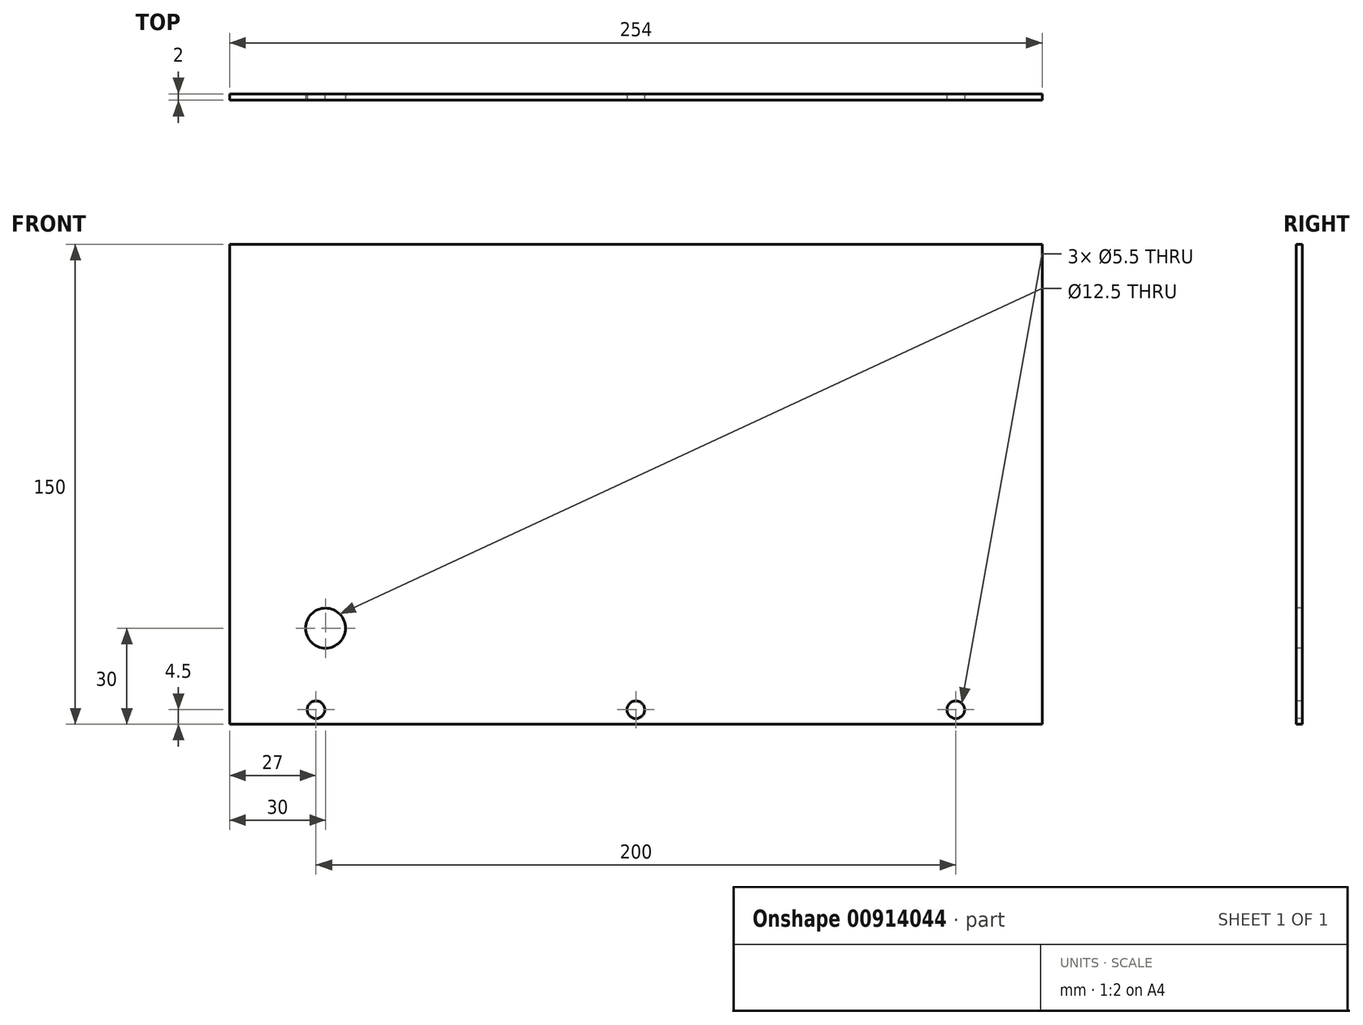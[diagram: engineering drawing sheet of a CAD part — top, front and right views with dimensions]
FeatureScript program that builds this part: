
annotation { "Feature Type Name" : "Feature", "Feature Type Description" : "" }
export const myFeature = defineFeature(function(context is Context, id is Id, definition is map)
    precondition{}
    {
        {
            var Q0;
            Q0=qCreatedBy(makeId("Front.planeOp"),FACE);
            var sketch = newSketch(context, id + "F0", { "sketchPlane" : qUnion([Q0])});
            skLineSegment(sketch, "E0.bottom", {"start": v(-127, 75) * mm, "end": v(127, 75) * mm});
            skLineSegment(sketch, "E0.top", {"start": v(-127, -75) * mm, "end": v(127, -75) * mm});
            skLineSegment(sketch, "E0.left", {"start": v(-127, 75) * mm, "end": v(-127, -75) * mm});
            skLineSegment(sketch, "E0.right", {"start": v(127, 75) * mm, "end": v(127, -75) * mm});
            skPoint(sketch, "E0.middle", {"position": v(0, 0) * mm});
            skSolve(sketch);
        }
        {
            var Q0;
            Q0=makeQuery(id+"F0.imprint","IMPRINT",FACE,{"disambiguationData":[TD([[makeQuery(id+"F0.imprint","IMPRINT",EDGE,{"derivedFrom":sQuery(id+"F0.wireOp",EDGE,"E0.bottom")}),-1.0]])]});
            extrude(context, id + "F1", {"entities" : qUnion([Q0]), "depth" : 2 * mm, "offsetDistance" : 25 * mm});
        }
        {
            var Q0;
            Q0=makeQuery(id+"F1.opExtrude","CAP_FACE",FACE,{"disambiguationData":[OSD([sQuery(id+"F0.wireOp",EDGE,"E0.bottom"),sQuery(id+"F0.wireOp",EDGE,"E0.top"),sQuery(id+"F0.wireOp",EDGE,"E0.left"),sQuery(id+"F0.wireOp",EDGE,"E0.right")])],"isStart":false});
            var sketch = newSketch(context, id + "F2", { "sketchPlane" : qUnion([Q0])});
            skCircle(sketch, "E1", {"center": v(-97, -45) * mm, "radius": 6.25 * mm});
            skSolve(sketch);
        }
        {
            var Q0;
            Q0=makeQuery(id+"F2.imprint","IMPRINT",FACE,{"disambiguationData":[TD([[makeQuery(id+"F2.imprint","IMPRINT",EDGE,{"derivedFrom":sQuery(id+"F2.wireOp",EDGE,"E1")}),1.0]])]});
            extrude(context, id + "F3", {"entities" : qUnion([Q0]), "operationType" : NewBodyOperationType.REMOVE, "oppositeDirection" : true, "depth" : 25 * mm, "offsetDistance" : 25 * mm});
        }
        {
            var Q0;
            Q0=makeQuery(id+"F1.opExtrude","CAP_FACE",FACE,{"disambiguationData":[OSD([sQuery(id+"F0.wireOp",EDGE,"E0.bottom"),sQuery(id+"F0.wireOp",EDGE,"E0.top"),sQuery(id+"F0.wireOp",EDGE,"E0.left"),sQuery(id+"F0.wireOp",EDGE,"E0.right")])],"isStart":false});
            var sketch = newSketch(context, id + "F4", { "sketchPlane" : qUnion([Q0])});
            skLineSegment(sketch, "E2", {"start": v(-127, -70.5) * mm, "end": v(-100, -70.5) * mm});
            skLineSegment(sketch, "E3", {"start": v(-100, -70.5) * mm, "end": v(0, -70.5) * mm});
            skLineSegment(sketch, "E4", {"start": v(0, -70.5) * mm, "end": v(100, -70.5) * mm});
            skLineSegment(sketch, "E5", {"start": v(0, -70.5) * mm, "end": v(0, -75) * mm});
            skSolve(sketch);
        }
        {
            var Q0;
            Q0=sQuery(id+"F4.wireOp",VERTEX,"E2.end");
            var Q1;
            Q1=sQuery(id+"F4.wireOp",VERTEX,"E3.end");
            var Q2;
            Q2=sQuery(id+"F4.wireOp",VERTEX,"E4.end");
            var Q3;
            Q3=makeQuery(id+"F1.opExtrude","SWEPT_BODY",BODY,{"disambiguationData":[OSD([sQuery(id+"F0.wireOp",EDGE,"E0.bottom"),sQuery(id+"F0.wireOp",EDGE,"E0.top"),sQuery(id+"F0.wireOp",EDGE,"E0.left"),sQuery(id+"F0.wireOp",EDGE,"E0.right")])]});
            hole(context, id + "F5", {"style" : HoleStyle.SIMPLE, "endStyle" : HoleEndStyle.BLIND, "standardTappedOrClearance" : lookupTablePath({ "fit" : "Normal", "standard" : "ISO", "size" : "M5", "type" : "Clearance" }), "standardBlindInLast" : lookupTablePath({ "fit" : "Normal", "standard" : "ISO", "size" : "M5", "type" : "Clearance" }), "holeDiameter" : 5.5 * mm, "majorDiameter" : 5 * mm, "holeDepth" : 13 * mm, "isTappedThrough" : true, "tappedDepth" : 10 * mm, "tapClearance" : 3, "startFromSketch" : true, "locations" : qUnion([Q0, Q1, Q2]), "scope" : qUnion([Q3])});
        }
    });
